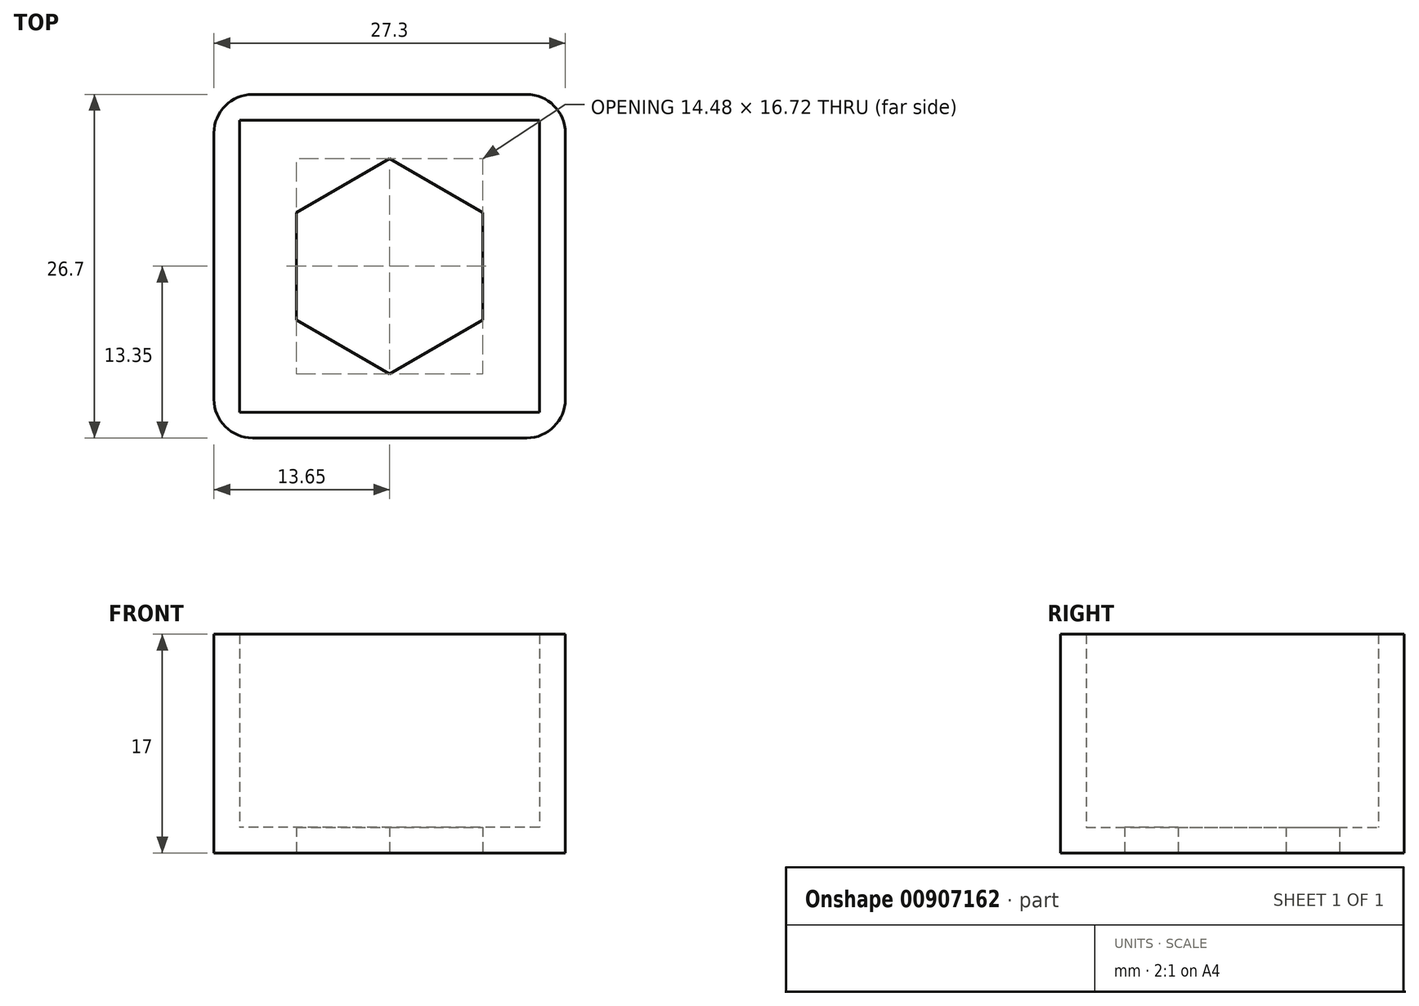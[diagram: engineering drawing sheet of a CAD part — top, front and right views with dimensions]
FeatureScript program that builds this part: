
annotation { "Feature Type Name" : "Feature", "Feature Type Description" : "" }
export const myFeature = defineFeature(function(context is Context, id is Id, definition is map)
    precondition{}
    {
        {
            var Q0;
            Q0=qCreatedBy(makeId("Top.planeOp"),FACE);
            var sketch = newSketch(context, id + "F0", { "sketchPlane" : qUnion([Q0])});
            skLineSegment(sketch, "E0.bottom", {"start": v(0, 0) * mm, "end": v(-23.3, 0) * mm});
            skLineSegment(sketch, "E0.top", {"start": v(0, 22.7) * mm, "end": v(-23.3, 22.7) * mm});
            skLineSegment(sketch, "E0.left", {"start": v(0, 0) * mm, "end": v(0, 22.7) * mm});
            skLineSegment(sketch, "E0.right", {"start": v(-23.3, 0) * mm, "end": v(-23.3, 22.7) * mm});
            skSolve(sketch);
        }
        {
            var Q0;
            Q0=makeQuery(id+"F0.imprint","IMPRINT",FACE,{"disambiguationData":[TD([[makeQuery(id+"F0.imprint","IMPRINT",EDGE,{"derivedFrom":sQuery(id+"F0.wireOp",EDGE,"E0.bottom")}),-1.0]])]});
            extrude(context, id + "F1", {"entities" : qUnion([Q0]), "depth" : 15 * mm, "offsetDistance" : 25 * mm});
        }
        {
            var Q0;
            Q0=makeQuery(id+"F1.opExtrude","CAP_FACE",FACE,{"disambiguationData":[OSD([sQuery(id+"F0.wireOp",EDGE,"E0.bottom"),sQuery(id+"F0.wireOp",EDGE,"E0.top"),sQuery(id+"F0.wireOp",EDGE,"E0.left"),sQuery(id+"F0.wireOp",EDGE,"E0.right")])],"isStart":false});
            shell(context, id + "F2", {"entities" : qUnion([Q0]), "thickness" : 2 * mm, "oppositeDirection" : true});
        }
        {
            var Q0;
            Q0=makeQuery(id+"F1.opExtrude","SWEPT_EDGE",EDGE,{"disambiguationData":[OSD([sQuery(id+"F0.wireOp",EDGE,"E0.bottom"),sQuery(id+"F0.wireOp",EDGE,"E0.right")])]});
            var Q1;
            Q1=makeQuery(id+"F1.opExtrude","SWEPT_EDGE",EDGE,{"disambiguationData":[OSD([sQuery(id+"F0.wireOp",EDGE,"E0.bottom"),sQuery(id+"F0.wireOp",EDGE,"E0.left")])]});
            var Q2;
            Q2=makeQuery(id+"F1.opExtrude","SWEPT_EDGE",EDGE,{"disambiguationData":[OSD([sQuery(id+"F0.wireOp",EDGE,"E0.top"),sQuery(id+"F0.wireOp",EDGE,"E0.left")])]});
            var Q3;
            Q3=makeQuery(id+"F1.opExtrude","SWEPT_EDGE",EDGE,{"disambiguationData":[OSD([sQuery(id+"F0.wireOp",EDGE,"E0.top"),sQuery(id+"F0.wireOp",EDGE,"E0.right")])]});
            fillet(context, id + "F3", {"entities" : qUnion([Q0, Q1, Q2, Q3]), "radius" : 3 * mm, "tangentPropagation" : true, "allowEdgeOverflow" : false});
        }
        {
            var Q0;
            Q0=makeQuery(id+"F1.opExtrude","CAP_FACE",FACE,{"disambiguationData":[OSD([sQuery(id+"F0.wireOp",EDGE,"E0.bottom"),sQuery(id+"F0.wireOp",EDGE,"E0.top"),sQuery(id+"F0.wireOp",EDGE,"E0.left"),sQuery(id+"F0.wireOp",EDGE,"E0.right")])],"isStart":true});
            var sketch = newSketch(context, id + "F4", { "sketchPlane" : qUnion([Q0])});
            skCircle(sketch, "E1.cCircle", {"center": v(-11.65, -11.35) * mm, "radius": 8.36 * mm, "construction": true});
            skPoint(sketch, "E1.cCircle.centerSnap0", {"position": v(-11.65, 2) * mm});
            skPoint(sketch, "E1.cCircle.centerSnap1", {"position": v(2, -11.35) * mm});
            skPoint(sketch, "E1.cCircle.perimeterSnap0", {"position": v(-11.65, -24.7) * mm});
            skLineSegment(sketch, "E1.0", {"start": v(-11.65, -19.71) * mm, "end": v(-18.9, -15.53) * mm});
            skPoint(sketch, "E1.0.startSnap0", {"position": v(-11.65, -24.7) * mm});
            skLineSegment(sketch, "E1.1", {"start": v(-18.9, -15.53) * mm, "end": v(-18.9, -7.17) * mm});
            skLineSegment(sketch, "E1.2", {"start": v(-18.9, -7.17) * mm, "end": v(-11.65, -2.99) * mm});
            skLineSegment(sketch, "E1.3", {"start": v(-11.65, -2.99) * mm, "end": v(-4.4, -7.17) * mm});
            skLineSegment(sketch, "E1.4", {"start": v(-4.4, -7.17) * mm, "end": v(-4.4, -15.53) * mm});
            skLineSegment(sketch, "E1.5", {"start": v(-4.4, -15.53) * mm, "end": v(-11.65, -19.71) * mm});
            skSolve(sketch);
        }
        {
            var Q0;
            Q0=makeQuery(id+"F4.imprint","IMPRINT",FACE,{"disambiguationData":[TD([[makeQuery(id+"F4.imprint","IMPRINT",EDGE,{"derivedFrom":sQuery(id+"F4.wireOp",EDGE,"E1.0")}),-1.0]])]});
            extrude(context, id + "F5", {"entities" : qUnion([Q0]), "operationType" : NewBodyOperationType.REMOVE, "oppositeDirection" : true, "depth" : 25 * mm, "offsetDistance" : 25 * mm});
        }
    });
